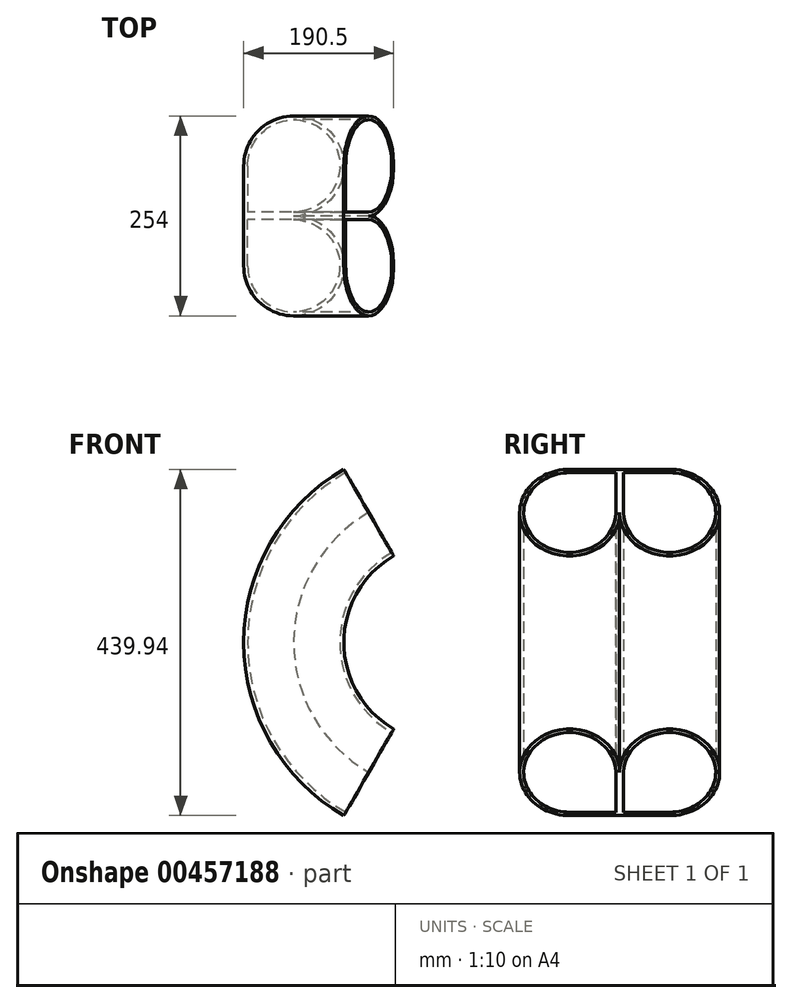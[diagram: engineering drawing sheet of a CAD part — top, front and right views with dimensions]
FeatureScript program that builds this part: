
annotation { "Feature Type Name" : "Feature", "Feature Type Description" : "" }
export const myFeature = defineFeature(function(context is Context, id is Id, definition is map)
    precondition{}
    {
        {
            var Q0;
            Q0=qCreatedBy(makeId("Top.planeOp"),FACE);
            var sketch = newSketch(context, id + "F0", { "sketchPlane" : qUnion([Q0])});
            skLineSegment(sketch, "E0.bottom", {"start": v(-76.2, 50.8) * mm, "end": v(177.8, 50.8) * mm});
            skLineSegment(sketch, "E0.top", {"start": v(-76.2, -101.6) * mm, "end": v(177.8, -101.6) * mm});
            skLineSegment(sketch, "E0.left", {"start": v(-76.2, 50.8) * mm, "end": v(-76.2, -101.6) * mm});
            skLineSegment(sketch, "E0.right", {"start": v(177.8, 50.8) * mm, "end": v(177.8, -101.6) * mm});
            skCircle(sketch, "E1", {"center": v(-12.7, -12.7) * mm, "radius": 63.5 * mm});
            skSolve(sketch);
        }
        {
            var Q0;
            {var subQ0=sQuery(id+"F0.wireOp",EDGE,"E0.left");var subQ1=sQuery(id+"F0.wireOp",EDGE,"E0.bottom");var subQ2=makeQuery(id+"F0.imprint","INTERSECT",VERTEX,{"derivedFrom":[subQ1,subQ0]});Q0=makeQuery(id+"F0.imprint","IMPRINT",FACE,{"disambiguationData":[TD([[makeQuery(id+"F0.imprint","IMPRINT",EDGE,{"disambiguationData":[TD([[subQ2,-1.0]])],"derivedFrom":subQ1}),-1.0]])]});}
            var Q1;
            {var subQ0=sQuery(id+"F0.wireOp",EDGE,"E1");var subQ1=makeQuery(id+"F0.imprint","INTERSECT",VERTEX,{"derivedFrom":[sQuery(id+"F0.wireOp",EDGE,"E0.bottom"),subQ0]});Q1=makeQuery(id+"F0.imprint","IMPRINT",FACE,{"disambiguationData":[TD([[makeQuery(id+"F0.imprint","IMPRINT",EDGE,{"disambiguationData":[TD([[subQ1,-1.0]])],"derivedFrom":subQ0}),1.0]])]});}
            var Q2;
            Q2=sQuery(id+"F0.wireOp",EDGE,"E0.right");
            revolve(context, id + "F1", {"entities" : qUnion([Q0, Q1]), "axis" : qUnion([Q2]), "revolveType" : RevolveType.SYMMETRIC, "angle" : 120 * degree});
        }
        {
            var Q0;
            Q0=makeQuery(id+"F1.opRevolve","CAP_FACE",FACE,{"disambiguationData":[OSD([sQuery(id+"F0.wireOp",EDGE,"E0.bottom"),sQuery(id+"F0.wireOp",EDGE,"E0.left"),sQuery(id+"F0.wireOp",EDGE,"E1")])],"isStart":true});
            var Q1;
            Q1=makeQuery(id+"F1.opRevolve","CAP_FACE",FACE,{"disambiguationData":[OSD([sQuery(id+"F0.wireOp",EDGE,"E0.bottom"),sQuery(id+"F0.wireOp",EDGE,"E0.left"),sQuery(id+"F0.wireOp",EDGE,"E1")])],"isStart":false});
            shell(context, id + "F2", {"entities" : qUnion([Q0, Q1]), "thickness" : 5 * mm});
        }
        {
            var Q0;
            Q0=makeQuery(id+"F1.opRevolve","SWEPT_FACE",FACE,{"disambiguationData":[OSD([sQuery(id+"F0.wireOp",EDGE,"E0.bottom")])]});
            cPlane(context, id + "F3", {"entities" : qUnion([Q0]), "cplaneType" : CPlaneType.OFFSET, "offset" : 0 * mm, "width" : 152.4 * mm, "height" : 152.4 * mm});
        }
        {
            var Q0;
            Q0=makeQuery(id+"F1.opRevolve","SWEPT_BODY",BODY,{"disambiguationData":[OSD([sQuery(id+"F0.wireOp",EDGE,"E0.bottom"),sQuery(id+"F0.wireOp",EDGE,"E0.left"),sQuery(id+"F0.wireOp",EDGE,"E1")])]});
            var Q1;
            Q1=qCreatedBy(id+"F3.planeOp",FACE);
            mirror(context, id + "F4", {"operationType" : NewBodyOperationType.ADD, "entities" : qUnion([Q0]), "mirrorPlane" : qUnion([Q1])});
        }
    });
